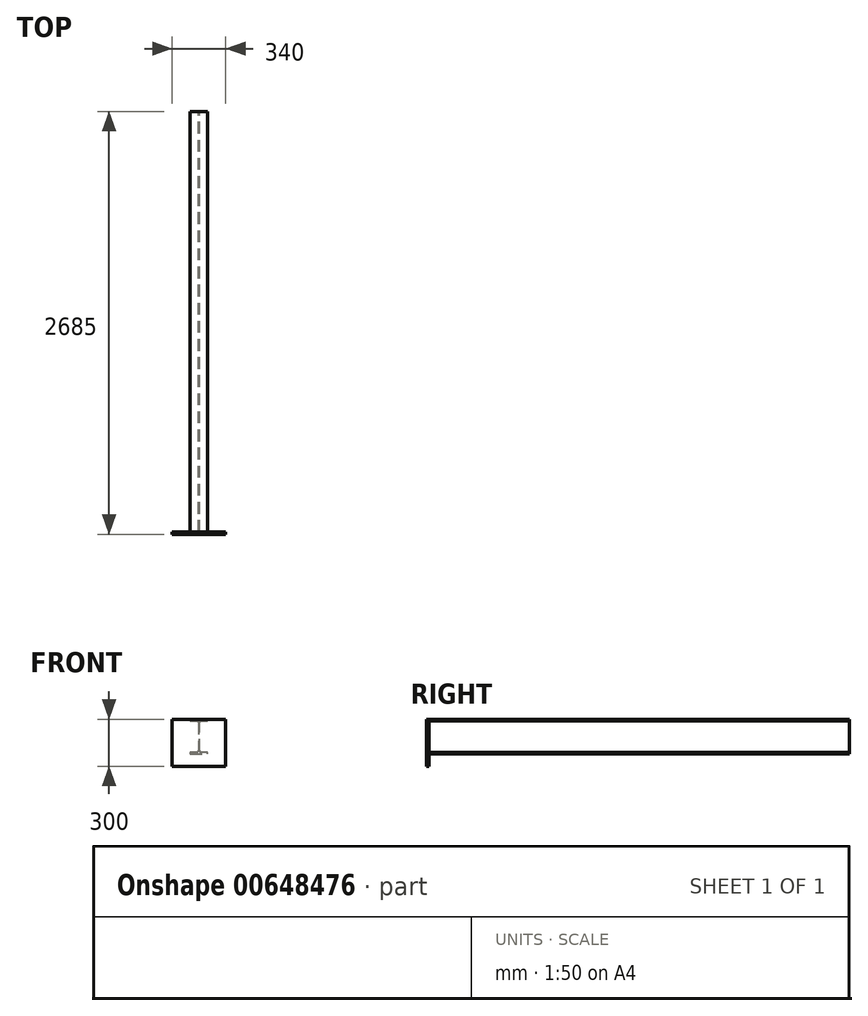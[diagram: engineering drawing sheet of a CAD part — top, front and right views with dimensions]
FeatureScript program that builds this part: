
annotation { "Feature Type Name" : "Feature", "Feature Type Description" : "" }
export const myFeature = defineFeature(function(context is Context, id is Id, definition is map)
    precondition{}
    {
        {
            var Q0;
            Q0=qCreatedBy(makeId("Front.planeOp"),FACE);
            var sketch = newSketch(context, id + "F0", { "sketchPlane" : qUnion([Q0])});
            skLineSegment(sketch, "E0", {"start": v(-55, -110) * mm, "end": v(0, -110) * mm});
            skLineSegment(sketch, "E1", {"start": v(0, -110) * mm, "end": v(55, -110) * mm});
            skLineSegment(sketch, "E2", {"start": v(55, -110) * mm, "end": v(55, -100.8) * mm});
            skLineSegment(sketch, "E3", {"start": v(55, -100.8) * mm, "end": v(14.95, -100.8) * mm});
            skArc(sketch, "E4", {"start": v(14.95, -100.8) * mm, "mid": v(6.46, -97.29) * mm, "end": v(2.95, -88.8) * mm});
            skLineSegment(sketch, "E5", {"start": v(2.95, -88.8) * mm, "end": v(2.95, 0) * mm});
            skLineSegment(sketch, "E6", {"start": v(2.95, 0) * mm, "end": v(2.95, 88.8) * mm});
            skArc(sketch, "E7", {"start": v(2.95, 88.8) * mm, "mid": v(6.46, 97.29) * mm, "end": v(14.95, 100.8) * mm});
            skLineSegment(sketch, "E8", {"start": v(14.95, 100.8) * mm, "end": v(55, 100.8) * mm});
            skLineSegment(sketch, "E9", {"start": v(55, 100.8) * mm, "end": v(55, 110) * mm});
            skLineSegment(sketch, "E10", {"start": v(55, 110) * mm, "end": v(0, 110) * mm});
            skLineSegment(sketch, "E11", {"start": v(0, 110) * mm, "end": v(-55, 110) * mm});
            skLineSegment(sketch, "E12", {"start": v(-55, 110) * mm, "end": v(-55, 100.8) * mm});
            skLineSegment(sketch, "E13", {"start": v(-55, 100.8) * mm, "end": v(-14.95, 100.8) * mm});
            skArc(sketch, "E14", {"start": v(-14.95, 100.8) * mm, "mid": v(-6.46, 97.29) * mm, "end": v(-2.95, 88.8) * mm});
            skLineSegment(sketch, "E15", {"start": v(-2.95, 88.8) * mm, "end": v(-2.95, 0) * mm});
            skLineSegment(sketch, "E16", {"start": v(-2.95, 0) * mm, "end": v(-2.95, -88.8) * mm});
            skArc(sketch, "E17", {"start": v(-2.95, -88.8) * mm, "mid": v(-6.46, -97.29) * mm, "end": v(-14.95, -100.8) * mm});
            skLineSegment(sketch, "E18", {"start": v(-14.95, -100.8) * mm, "end": v(-55, -100.8) * mm});
            skLineSegment(sketch, "E19", {"start": v(-55, -100.8) * mm, "end": v(-55, -110) * mm});
            skSolve(sketch);
        }
        {
            var Q0;
            Q0=makeQuery(id+"F0.imprint","IMPRINT",FACE,{"disambiguationData":[TD([[makeQuery(id+"F0.imprint","IMPRINT",EDGE,{"derivedFrom":sQuery(id+"F0.wireOp",EDGE,"E0")}),1.0]])]});
            extrude(context, id + "F1", {"entities" : qUnion([Q0]), "endBound" : BoundingType.SYMMETRIC, "depth" : 2670 * mm, "offsetDistance" : 25 * mm});
        }
        {
            var Q0;
            Q0=makeQuery(id+"F1.opExtrude","CAP_FACE",FACE,{"disambiguationData":[OSD([sQuery(id+"F0.wireOp",EDGE,"E0"),sQuery(id+"F0.wireOp",EDGE,"E1"),sQuery(id+"F0.wireOp",EDGE,"E2"),sQuery(id+"F0.wireOp",EDGE,"E3"),sQuery(id+"F0.wireOp",EDGE,"E4"),sQuery(id+"F0.wireOp",EDGE,"E5"),sQuery(id+"F0.wireOp",EDGE,"E6"),sQuery(id+"F0.wireOp",EDGE,"E7"),sQuery(id+"F0.wireOp",EDGE,"E8"),sQuery(id+"F0.wireOp",EDGE,"E9"),sQuery(id+"F0.wireOp",EDGE,"E10"),sQuery(id+"F0.wireOp",EDGE,"E11"),sQuery(id+"F0.wireOp",EDGE,"E12"),sQuery(id+"F0.wireOp",EDGE,"E13"),sQuery(id+"F0.wireOp",EDGE,"E14"),sQuery(id+"F0.wireOp",EDGE,"E15"),sQuery(id+"F0.wireOp",EDGE,"E16"),sQuery(id+"F0.wireOp",EDGE,"E17"),sQuery(id+"F0.wireOp",EDGE,"E18"),sQuery(id+"F0.wireOp",EDGE,"E19")])],"isStart":false});
            var sketch = newSketch(context, id + "F2", { "sketchPlane" : qUnion([Q0])});
            skLineSegment(sketch, "E20.bottom", {"start": v(-170, 110) * mm, "end": v(170, 110) * mm});
            skLineSegment(sketch, "E20.top", {"start": v(-170, -190) * mm, "end": v(170, -190) * mm});
            skLineSegment(sketch, "E20.left", {"start": v(-170, 110) * mm, "end": v(-170, -190) * mm});
            skLineSegment(sketch, "E20.right", {"start": v(170, 110) * mm, "end": v(170, -190) * mm});
            skPoint(sketch, "E21", {"position": v(100, 60) * mm});
            skPoint(sketch, "E22", {"position": v(100, -140) * mm});
            skPoint(sketch, "E23", {"position": v(-100, 60) * mm});
            skPoint(sketch, "E24", {"position": v(-100, -140) * mm});
            skSolve(sketch);
        }
        {
            var Q0;
            Q0 = qSketchRegion(id + "F2", true);
            var Q1;
            Q1=makeQuery(id+"F2.imprint","IMPRINT",FACE,{"disambiguationData":[TD([[makeQuery(id+"F2.imprint","IMPRINT",EDGE,{"derivedFrom":sQuery(id+"F2.wireOp",EDGE,"E20.top")}),1.0]])]});
            extrude(context, id + "F3", {"entities" : qUnion([Q0, Q1]), "depth" : 15 * mm, "offsetDistance" : 25 * mm});
        }
    });
